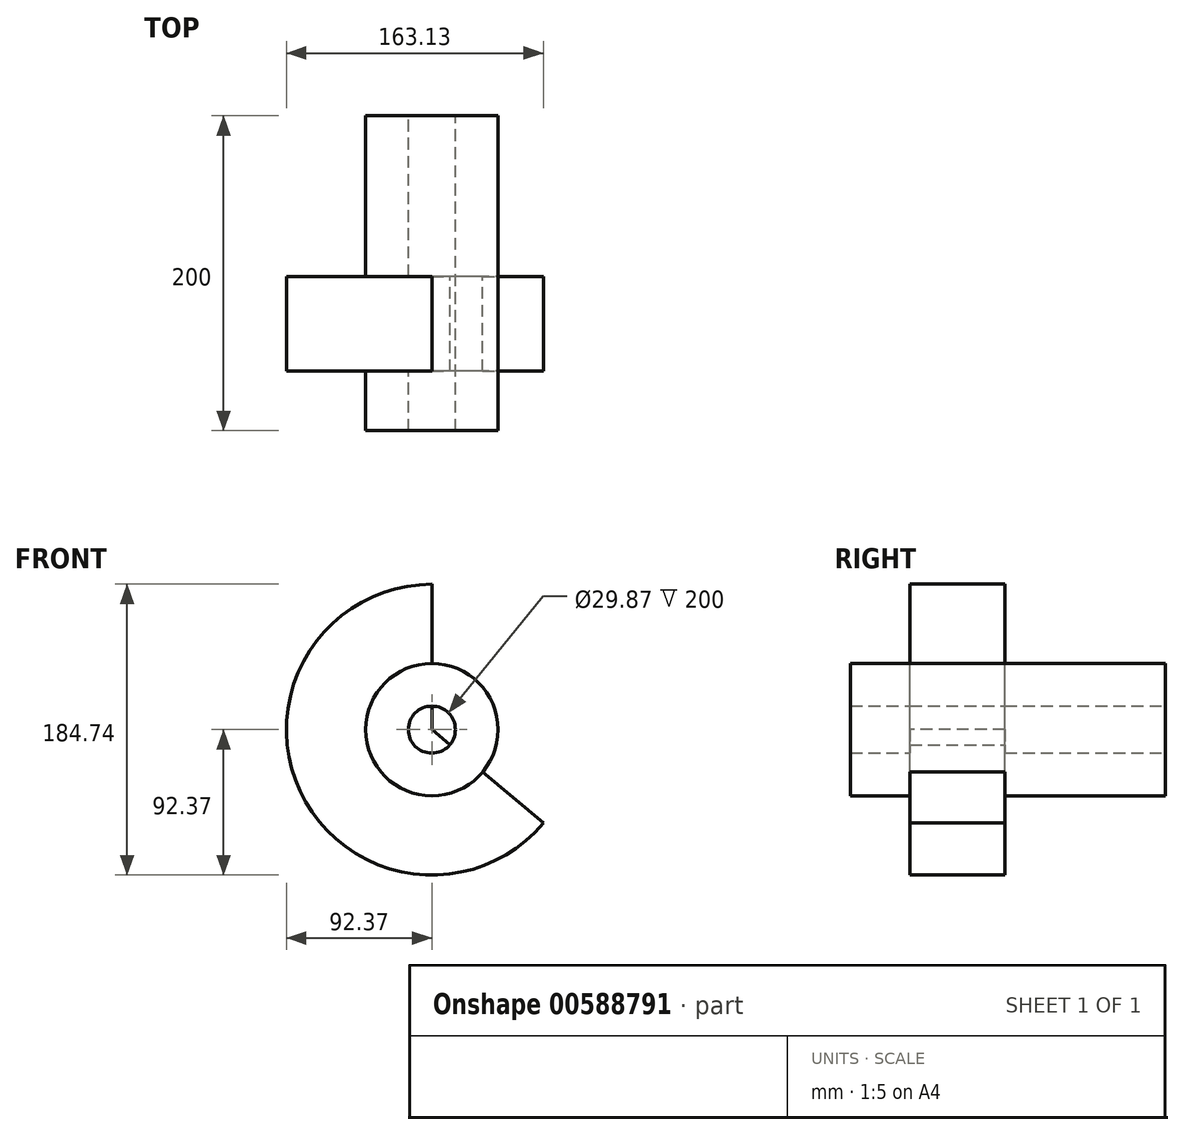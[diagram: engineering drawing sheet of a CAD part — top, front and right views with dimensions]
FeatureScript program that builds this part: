
annotation { "Feature Type Name" : "Feature", "Feature Type Description" : "" }
export const myFeature = defineFeature(function(context is Context, id is Id, definition is map)
    precondition{}
    {
        {
            var Q0;
            Q0=qCreatedBy(makeId("Front.planeOp"),FACE);
            var sketch = newSketch(context, id + "F0", { "sketchPlane" : qUnion([Q0])});
            skCircle(sketch, "E0", {"center": v(0, 0) * mm, "radius": 42.01 * mm});
            skCircle(sketch, "E1", {"center": v(0, 0) * mm, "radius": 14.93 * mm});
            skSolve(sketch);
        }
        {
            var Q0;
            Q0 = qSketchRegion(id + "F0", true);
            extrude(context, id + "F1", {"entities" : qUnion([Q0]), "depth" : 200 * mm, "offsetDistance" : 25 * mm});
        }
        {
            var Q0;
            Q0=qCreatedBy(makeId("Right.planeOp"),FACE);
            var sketch = newSketch(context, id + "F2", { "sketchPlane" : qUnion([Q0])});
            skLineSegment(sketch, "E2.bottom", {"start": v(0, 0) * mm, "end": v(-101.93, 0) * mm});
            skLineSegment(sketch, "E2.top", {"start": v(0, 63.5) * mm, "end": v(-101.93, 63.5) * mm});
            skLineSegment(sketch, "E2.left", {"start": v(0, 0) * mm, "end": v(0, 63.5) * mm});
            skLineSegment(sketch, "E2.right", {"start": v(-101.93, 0) * mm, "end": v(-101.93, 63.5) * mm});
            skLineSegment(sketch, "E3.bottom", {"start": v(-101.93, 63.5) * mm, "end": v(-98.5, 63.5) * mm});
            skLineSegment(sketch, "E3.top", {"start": v(-101.93, 63.5) * mm, "end": v(-98.5, 63.5) * mm});
            skLineSegment(sketch, "E3.left", {"start": v(-101.93, 63.5) * mm, "end": v(-101.93, 63.5) * mm});
            skLineSegment(sketch, "E3.right", {"start": v(-98.5, 63.5) * mm, "end": v(-98.5, 63.5) * mm});
            skLineSegment(sketch, "E4.bottom", {"start": v(-101.93, 0) * mm, "end": v(-162.13, 0) * mm});
            skLineSegment(sketch, "E4.top", {"start": v(-101.93, 92.37) * mm, "end": v(-162.13, 92.37) * mm});
            skLineSegment(sketch, "E4.left", {"start": v(-101.93, 0) * mm, "end": v(-101.93, 92.37) * mm});
            skLineSegment(sketch, "E4.right", {"start": v(-162.13, 0) * mm, "end": v(-162.13, 92.37) * mm});
            skSolve(sketch);
        }
        {
            var Q0;
            {var subQ3=sQuery(id+"F2.wireOp",EDGE,"E4.bottom");Q0=makeQuery(id+"F2.imprint","IMPRINT",FACE,{"disambiguationData":[TD([[makeQuery(id+"F2.imprint","IMPRINT",EDGE,{"derivedFrom":subQ3}),-1.0]])]});}
            var Q1;
            Q1=sQuery(id+"F2.wireOp",EDGE,"E4.bottom");
            revolve(context, id + "F3", {"operationType" : NewBodyOperationType.ADD, "entities" : qUnion([Q0]), "axis" : qUnion([Q1]), "revolveType" : RevolveType.ONE_DIRECTION, "angle" : 230 * degree});
        }
    });
